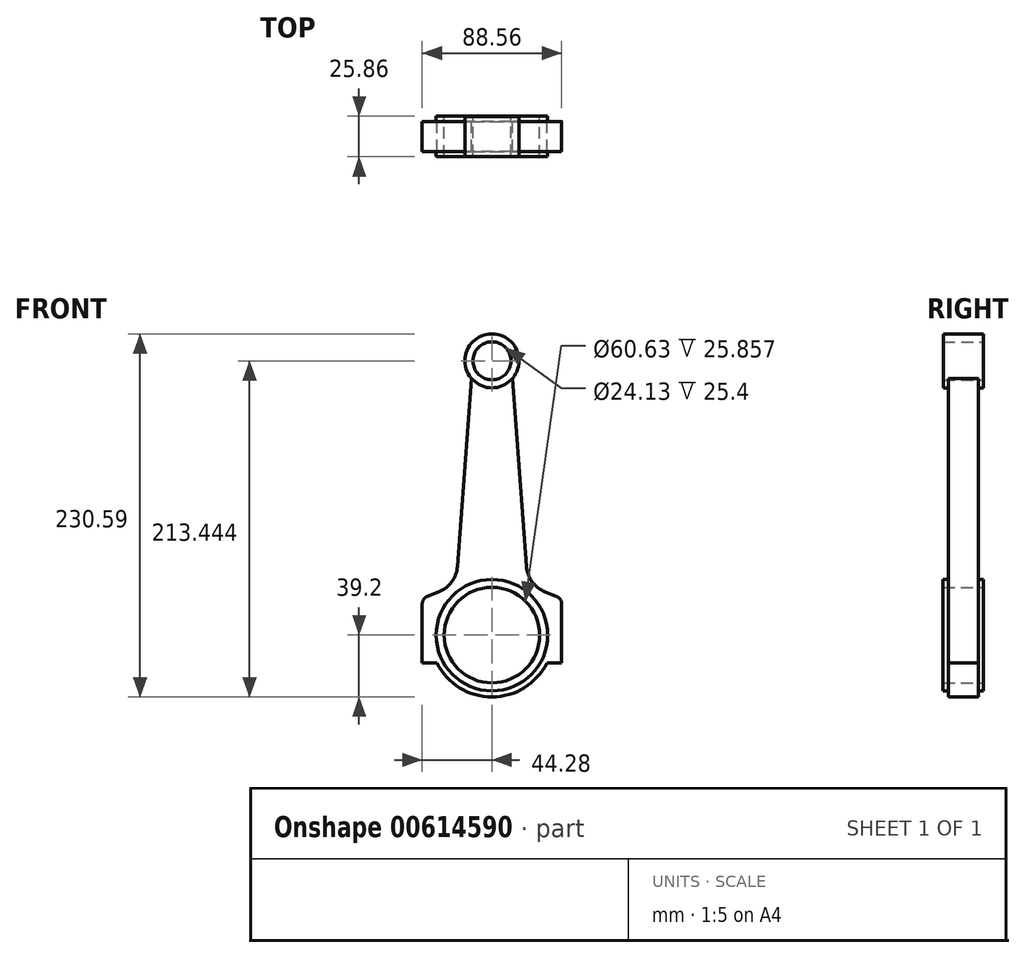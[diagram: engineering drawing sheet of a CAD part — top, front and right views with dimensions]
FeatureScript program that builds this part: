
annotation { "Feature Type Name" : "Feature", "Feature Type Description" : "" }
export const myFeature = defineFeature(function(context is Context, id is Id, definition is map)
    precondition{}
    {
        {
            var Q0;
            Q0=qCreatedBy(makeId("Front.planeOp"),FACE);
            var sketch = newSketch(context, id + "F0", { "sketchPlane" : qUnion([Q0])});
            skLineSegment(sketch, "E0", {"start": v(0, 104.96) * mm, "end": v(0, -69.28) * mm, "construction": true});
            skCircle(sketch, "E1", {"center": v(0, -69.28) * mm, "radius": 30.31 * mm});
            skCircle(sketch, "E2.0", {"center": v(0, -69.28) * mm, "radius": 35.4 * mm});
            skCircle(sketch, "E3.0", {"center": v(0, -69.28) * mm, "radius": 39.2 * mm});
            skLineSegment(sketch, "E4", {"start": v(0, -69.28) * mm, "end": v(-44.28, -69.28) * mm});
            skCircle(sketch, "E5", {"center": v(0, 104.96) * mm, "radius": 12.07 * mm});
            skCircle(sketch, "E6.0", {"center": v(0, 104.96) * mm, "radius": 17.14 * mm});
            skLineSegment(sketch, "E7", {"start": v(-44.28, -69.28) * mm, "end": v(-44.28, -49.47) * mm});
            skLineSegment(sketch, "E8.MirrorCS", {"start": v(44.28, -69.28) * mm, "end": v(44.28, -49.47) * mm});
            skLineSegment(sketch, "E9.MirrorCS", {"start": v(0, -69.28) * mm, "end": v(44.28, -69.28) * mm});
            skLineSegment(sketch, "E10", {"start": v(44.28, -69.28) * mm, "end": v(44.28, -87.06) * mm});
            skLineSegment(sketch, "E11", {"start": v(44.28, -87.06) * mm, "end": v(34.94, -87.06) * mm});
            skLineSegment(sketch, "E12.MirrorCS", {"start": v(-44.28, -69.28) * mm, "end": v(-44.28, -87.06) * mm});
            skLineSegment(sketch, "E13.MirrorCS", {"start": v(-44.28, -87.06) * mm, "end": v(-34.94, -87.06) * mm});
            skLineSegment(sketch, "E14", {"start": v(-41.1, -44.75) * mm, "end": v(-33.82, -41.82) * mm});
            skLineSegment(sketch, "E15", {"start": v(-21.93, -25.58) * mm, "end": v(-12.95, 93.72) * mm});
            skLineSegment(sketch, "E16.MirrorCS", {"start": v(21.93, -25.58) * mm, "end": v(12.95, 93.72) * mm});
            skLineSegment(sketch, "E17.MirrorCS", {"start": v(41.1, -44.75) * mm, "end": v(33.82, -41.82) * mm});
            skPoint(sketch, "E18.visualSharp", {"position": v(-22.82, -37.4) * mm});
            skArc(sketch, "E18.filletArc", {"start": v(-33.82, -41.82) * mm, "mid": v(-25.55, -35.4) * mm, "end": v(-21.93, -25.58) * mm});
            skPoint(sketch, "E19.visualSharp", {"position": v(22.82, -37.4) * mm});
            skArc(sketch, "E19.filletArc", {"start": v(21.93, -25.58) * mm, "mid": v(25.55, -35.4) * mm, "end": v(33.82, -41.82) * mm});
            skPoint(sketch, "E20.visualSharp", {"position": v(-44.28, -46.03) * mm});
            skArc(sketch, "E20.filletArc", {"start": v(-41.1, -44.75) * mm, "mid": v(-43.41, -46.62) * mm, "end": v(-44.28, -49.47) * mm});
            skPoint(sketch, "E21.visualSharp", {"position": v(44.28, -46.03) * mm});
            skArc(sketch, "E21.filletArc", {"start": v(44.28, -49.47) * mm, "mid": v(43.41, -46.62) * mm, "end": v(41.1, -44.75) * mm});
            skSolve(sketch);
        }
        {
            var Q0;
            {var subQ0=sQuery(id+"F0.wireOp",EDGE,"E4");var subQ1=sQuery(id+"F0.wireOp",EDGE,"E1");var subQ2=makeQuery(id+"F0.imprint","INTERSECT",VERTEX,{"derivedFrom":[subQ1,subQ0]});Q0=makeQuery(id+"F0.imprint","IMPRINT",FACE,{"disambiguationData":[TD([[makeQuery(id+"F0.imprint","IMPRINT",EDGE,{"disambiguationData":[TD([[subQ2,1.0]])],"derivedFrom":subQ1}),-1.0]])]});}
            extrude(context, id + "F1", {"entities" : qUnion([Q0]), "endBound" : BoundingType.SYMMETRIC, "depth" : 25.86 * mm, "offsetDistance" : 25.4 * mm});
        }
        {
            var Q0;
            {var subQ7=sQuery(id+"F0.wireOp",EDGE,"E7");Q0=makeQuery(id+"F0.imprint","IMPRINT",FACE,{"disambiguationData":[TD([[makeQuery(id+"F0.imprint","IMPRINT",EDGE,{"derivedFrom":subQ7}),-1.0]])]});}
            var Q1;
            {var subQ0=sQuery(id+"F0.wireOp",EDGE,"E4");var subQ1=sQuery(id+"F0.wireOp",EDGE,"E2.0");var subQ2=makeQuery(id+"F0.imprint","INTERSECT",VERTEX,{"derivedFrom":[subQ1,subQ0]});Q1=makeQuery(id+"F0.imprint","IMPRINT",FACE,{"disambiguationData":[TD([[makeQuery(id+"F0.imprint","IMPRINT",EDGE,{"disambiguationData":[TD([[subQ2,1.0]])],"derivedFrom":subQ1}),-1.0]])]});}
            extrude(context, id + "F2", {"entities" : qUnion([Q0, Q1]), "operationType" : NewBodyOperationType.ADD, "endBound" : BoundingType.SYMMETRIC, "depth" : 19.05 * mm, "offsetDistance" : 25.4 * mm});
        }
        {
            var Q0;
            {var subQ0=sQuery(id+"F0.wireOp",EDGE,"E4");var subQ1=sQuery(id+"F0.wireOp",EDGE,"E1");var subQ2=makeQuery(id+"F0.imprint","INTERSECT",VERTEX,{"derivedFrom":[subQ1,subQ0]});Q0=makeQuery(id+"F0.imprint","IMPRINT",FACE,{"disambiguationData":[TD([[makeQuery(id+"F0.imprint","IMPRINT",EDGE,{"disambiguationData":[TD([[subQ2,-1.0]])],"derivedFrom":subQ1}),-1.0]])]});}
            extrude(context, id + "F3", {"entities" : qUnion([Q0]), "endBound" : BoundingType.SYMMETRIC, "depth" : 25.86 * mm, "offsetDistance" : 25.4 * mm});
        }
        {
            var Q0;
            {var subQ4=sQuery(id+"F0.wireOp",EDGE,"E12.MirrorCS");Q0=makeQuery(id+"F0.imprint","IMPRINT",FACE,{"disambiguationData":[TD([[makeQuery(id+"F0.imprint","IMPRINT",EDGE,{"derivedFrom":subQ4}),1.0]])]});}
            var Q1;
            {var subQ5=sQuery(id+"F0.wireOp",EDGE,"E4");var subQ7=sQuery(id+"F0.wireOp",EDGE,"E2.0");var subQ8=makeQuery(id+"F0.imprint","INTERSECT",VERTEX,{"derivedFrom":[subQ7,subQ5]});Q1=makeQuery(id+"F0.imprint","IMPRINT",FACE,{"disambiguationData":[TD([[makeQuery(id+"F0.imprint","IMPRINT",EDGE,{"disambiguationData":[TD([[subQ8,-1.0]])],"derivedFrom":subQ7}),-1.0]])]});}
            var Q2;
            {var subQ4=sQuery(id+"F0.wireOp",EDGE,"E10");Q2=makeQuery(id+"F0.imprint","IMPRINT",FACE,{"disambiguationData":[TD([[makeQuery(id+"F0.imprint","IMPRINT",EDGE,{"derivedFrom":subQ4}),-1.0]])]});}
            extrude(context, id + "F4", {"entities" : qUnion([Q0, Q1, Q2]), "operationType" : NewBodyOperationType.ADD, "endBound" : BoundingType.SYMMETRIC, "depth" : 19.05 * mm, "offsetDistance" : 25.4 * mm});
        }
        {
            var Q0;
            Q0=makeQuery(id+"F0.imprint","IMPRINT",FACE,{"disambiguationData":[TD([[makeQuery(id+"F0.imprint","IMPRINT",EDGE,{"derivedFrom":sQuery(id+"F0.wireOp",EDGE,"E5")}),-1.0]])]});
            extrude(context, id + "F5", {"entities" : qUnion([Q0]), "operationType" : NewBodyOperationType.ADD, "endBound" : BoundingType.SYMMETRIC, "depth" : 25.4 * mm, "offsetDistance" : 25.4 * mm});
        }
    });
